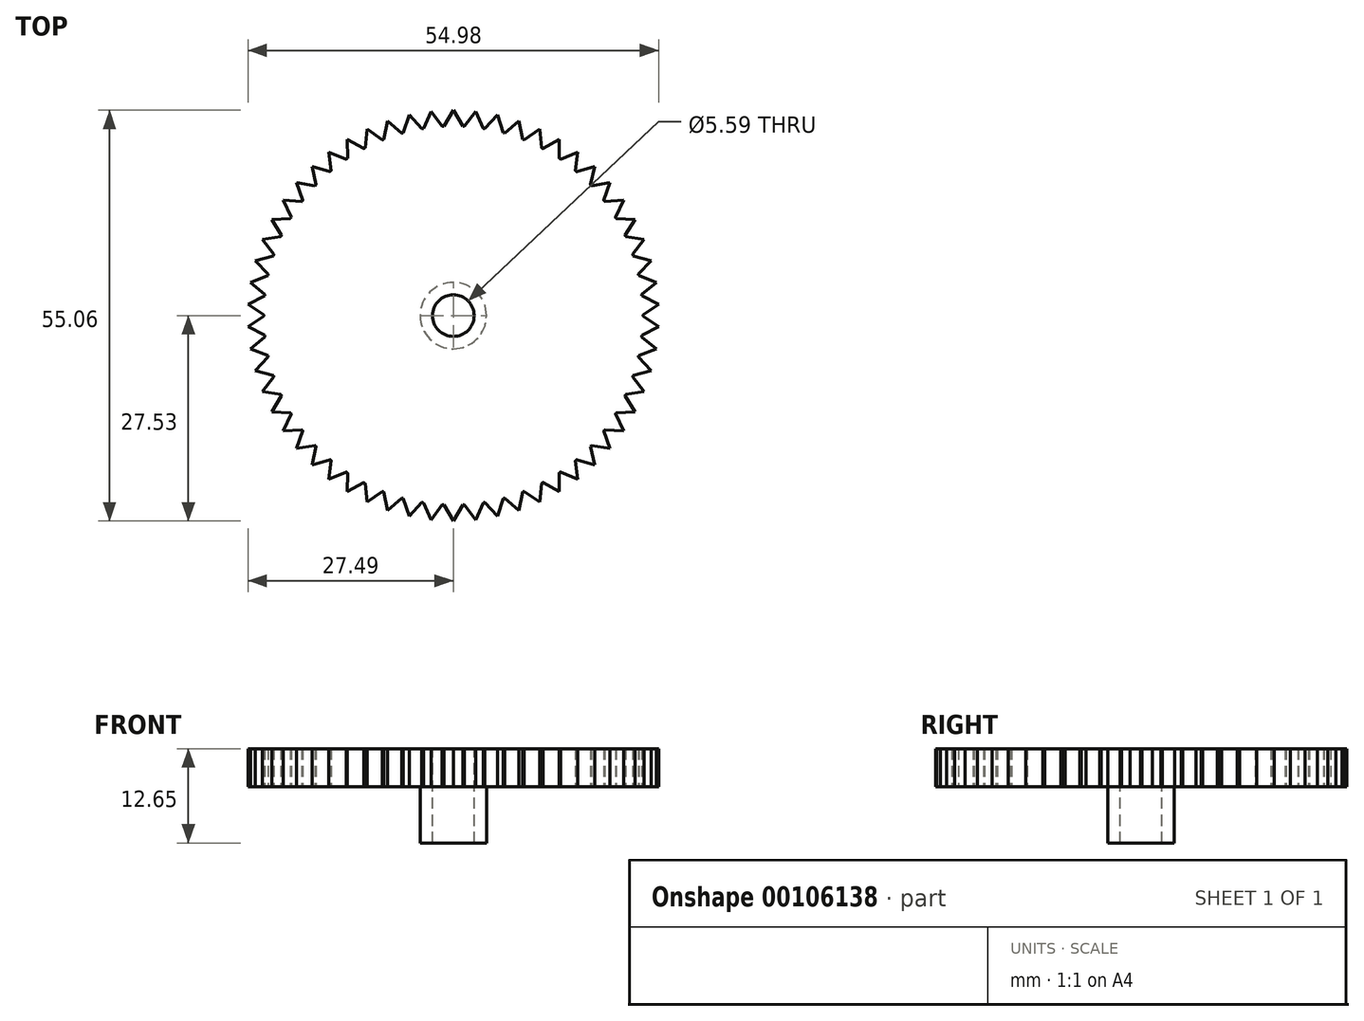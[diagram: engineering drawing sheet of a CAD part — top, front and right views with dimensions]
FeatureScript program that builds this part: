
annotation { "Feature Type Name" : "Feature", "Feature Type Description" : "" }
export const myFeature = defineFeature(function(context is Context, id is Id, definition is map)
    precondition{}
    {
        {
            var Q0;
            Q0=qCreatedBy(makeId("Top.planeOp"),FACE);
            var sketch = newSketch(context, id + "F0", { "sketchPlane" : qUnion([Q0])});
            skCircle(sketch, "E0", {"center": v(0, 0) * mm, "radius": 25.4 * mm});
            skLineSegment(sketch, "E1", {"start": v(-1.27, 25.37) * mm, "end": v(0, 27.53) * mm});
            skLineSegment(sketch, "E2", {"start": v(0, 27.53) * mm, "end": v(1.27, 25.37) * mm});
            skLineSegment(sketch, "E3.1.0", {"start": v(-4, 25.08) * mm, "end": v(-2.98, 27.37) * mm});
            skLineSegment(sketch, "E3.1.1", {"start": v(-2.98, 27.37) * mm, "end": v(-1.48, 25.36) * mm});
            skLineSegment(sketch, "E3.2.0", {"start": v(-6.7, 24.5) * mm, "end": v(-5.92, 26.88) * mm});
            skLineSegment(sketch, "E3.2.1", {"start": v(-5.92, 26.88) * mm, "end": v(-4.21, 25.05) * mm});
            skLineSegment(sketch, "E4.1.3.0", {"start": v(-9.3, 23.63) * mm, "end": v(-8.79, 26.09) * mm});
            skLineSegment(sketch, "E4.3.3.0", {"start": v(-8.79, 26.09) * mm, "end": v(-6.9, 24.45) * mm});
            skLineSegment(sketch, "E4.1.4.0", {"start": v(-11.8, 22.5) * mm, "end": v(-11.56, 24.98) * mm});
            skLineSegment(sketch, "E4.3.4.0", {"start": v(-11.56, 24.98) * mm, "end": v(-9.5, 23.56) * mm});
            skLineSegment(sketch, "E4.1.5.0", {"start": v(-14.17, 21.08) * mm, "end": v(-14.2, 23.59) * mm});
            skLineSegment(sketch, "E4.3.5.0", {"start": v(-14.2, 23.59) * mm, "end": v(-12, 22.4) * mm});
            skLineSegment(sketch, "E4.1.6.0", {"start": v(-16.36, 19.43) * mm, "end": v(-16.66, 21.91) * mm});
            skLineSegment(sketch, "E4.3.6.0", {"start": v(-16.66, 21.91) * mm, "end": v(-14.34, 20.96) * mm});
            skLineSegment(sketch, "E4.1.7.0", {"start": v(-18.37, 17.54) * mm, "end": v(-18.93, 19.99) * mm});
            skLineSegment(sketch, "E4.3.7.0", {"start": v(-18.93, 19.99) * mm, "end": v(-16.52, 19.3) * mm});
            skLineSegment(sketch, "E4.1.8.0", {"start": v(-20.16, 15.46) * mm, "end": v(-20.98, 17.82) * mm});
            skLineSegment(sketch, "E4.3.8.0", {"start": v(-20.98, 17.82) * mm, "end": v(-18.51, 17.4) * mm});
            skLineSegment(sketch, "E4.1.9.0", {"start": v(-21.7, 13.19) * mm, "end": v(-22.78, 15.45) * mm});
            skLineSegment(sketch, "E4.3.9.0", {"start": v(-22.78, 15.45) * mm, "end": v(-20.28, 15.29) * mm});
            skLineSegment(sketch, "E4.1.10.0", {"start": v(-23, 10.76) * mm, "end": v(-24.32, 12.9) * mm});
            skLineSegment(sketch, "E4.3.10.0", {"start": v(-24.32, 12.9) * mm, "end": v(-21.82, 13) * mm});
            skLineSegment(sketch, "E4.1.11.0", {"start": v(-24.04, 8.2) * mm, "end": v(-25.57, 10.19) * mm});
            skLineSegment(sketch, "E4.3.11.0", {"start": v(-25.57, 10.19) * mm, "end": v(-23.1, 10.57) * mm});
            skLineSegment(sketch, "E4.1.12.0", {"start": v(-24.78, 5.56) * mm, "end": v(-26.52, 7.36) * mm});
            skLineSegment(sketch, "E4.3.12.0", {"start": v(-26.52, 7.36) * mm, "end": v(-24.1, 8.01) * mm});
            skLineSegment(sketch, "E4.1.13.0", {"start": v(-25.24, 2.85) * mm, "end": v(-27.17, 4.45) * mm});
            skLineSegment(sketch, "E4.3.13.0", {"start": v(-27.17, 4.45) * mm, "end": v(-24.83, 5.36) * mm});
            skLineSegment(sketch, "E4.1.14.0", {"start": v(-25.4, 0.1) * mm, "end": v(-27.49, 1.5) * mm});
            skLineSegment(sketch, "E4.3.14.0", {"start": v(-27.49, 1.5) * mm, "end": v(-25.26, 2.64) * mm});
            skLineSegment(sketch, "E4.1.15.0", {"start": v(-25.26, -2.64) * mm, "end": v(-27.49, -1.5) * mm});
            skLineSegment(sketch, "E4.3.15.0", {"start": v(-27.49, -1.5) * mm, "end": v(-25.4, -0.1) * mm});
            skLineSegment(sketch, "E4.1.16.0", {"start": v(-24.83, -5.36) * mm, "end": v(-27.17, -4.45) * mm});
            skLineSegment(sketch, "E4.3.16.0", {"start": v(-27.17, -4.45) * mm, "end": v(-25.24, -2.85) * mm});
            skLineSegment(sketch, "E4.1.17.0", {"start": v(-24.1, -8.01) * mm, "end": v(-26.52, -7.36) * mm});
            skLineSegment(sketch, "E4.3.17.0", {"start": v(-26.52, -7.36) * mm, "end": v(-24.78, -5.56) * mm});
            skLineSegment(sketch, "E4.1.18.0", {"start": v(-23.1, -10.57) * mm, "end": v(-25.57, -10.19) * mm});
            skLineSegment(sketch, "E4.3.18.0", {"start": v(-25.57, -10.19) * mm, "end": v(-24.04, -8.2) * mm});
            skLineSegment(sketch, "E4.1.19.0", {"start": v(-21.82, -13) * mm, "end": v(-24.32, -12.9) * mm});
            skLineSegment(sketch, "E4.3.19.0", {"start": v(-24.32, -12.9) * mm, "end": v(-23, -10.76) * mm});
            skLineSegment(sketch, "E4.1.20.0", {"start": v(-20.28, -15.29) * mm, "end": v(-22.78, -15.45) * mm});
            skLineSegment(sketch, "E4.3.20.0", {"start": v(-22.78, -15.45) * mm, "end": v(-21.7, -13.19) * mm});
            skLineSegment(sketch, "E4.1.21.0", {"start": v(-18.51, -17.4) * mm, "end": v(-20.98, -17.82) * mm});
            skLineSegment(sketch, "E4.3.21.0", {"start": v(-20.98, -17.82) * mm, "end": v(-20.16, -15.46) * mm});
            skLineSegment(sketch, "E4.1.22.0", {"start": v(-16.52, -19.3) * mm, "end": v(-18.93, -19.99) * mm});
            skLineSegment(sketch, "E4.3.22.0", {"start": v(-18.93, -19.99) * mm, "end": v(-18.37, -17.54) * mm});
            skLineSegment(sketch, "E4.1.23.0", {"start": v(-14.34, -20.96) * mm, "end": v(-16.66, -21.91) * mm});
            skLineSegment(sketch, "E4.3.23.0", {"start": v(-16.66, -21.91) * mm, "end": v(-16.36, -19.43) * mm});
            skLineSegment(sketch, "E4.1.24.0", {"start": v(-12, -22.4) * mm, "end": v(-14.2, -23.59) * mm});
            skLineSegment(sketch, "E4.3.24.0", {"start": v(-14.2, -23.59) * mm, "end": v(-14.17, -21.08) * mm});
            skLineSegment(sketch, "E4.1.25.0", {"start": v(-9.5, -23.56) * mm, "end": v(-11.56, -24.98) * mm});
            skLineSegment(sketch, "E4.3.25.0", {"start": v(-11.56, -24.98) * mm, "end": v(-11.8, -22.5) * mm});
            skLineSegment(sketch, "E4.1.26.0", {"start": v(-6.9, -24.45) * mm, "end": v(-8.79, -26.09) * mm});
            skLineSegment(sketch, "E4.3.26.0", {"start": v(-8.79, -26.09) * mm, "end": v(-9.3, -23.63) * mm});
            skLineSegment(sketch, "E4.1.27.0", {"start": v(-4.21, -25.05) * mm, "end": v(-5.92, -26.88) * mm});
            skLineSegment(sketch, "E4.3.27.0", {"start": v(-5.92, -26.88) * mm, "end": v(-6.7, -24.5) * mm});
            skLineSegment(sketch, "E4.1.28.0", {"start": v(-1.48, -25.36) * mm, "end": v(-2.98, -27.37) * mm});
            skLineSegment(sketch, "E4.3.28.0", {"start": v(-2.98, -27.37) * mm, "end": v(-4, -25.08) * mm});
            skLineSegment(sketch, "E4.1.29.0", {"start": v(1.27, -25.37) * mm, "end": v(0, -27.53) * mm});
            skLineSegment(sketch, "E4.3.29.0", {"start": v(0, -27.53) * mm, "end": v(-1.27, -25.37) * mm});
            skLineSegment(sketch, "E4.1.30.0", {"start": v(4, -25.08) * mm, "end": v(2.98, -27.37) * mm});
            skLineSegment(sketch, "E4.3.30.0", {"start": v(2.98, -27.37) * mm, "end": v(1.48, -25.36) * mm});
            skLineSegment(sketch, "E4.1.31.0", {"start": v(6.7, -24.5) * mm, "end": v(5.92, -26.88) * mm});
            skLineSegment(sketch, "E4.3.31.0", {"start": v(5.92, -26.88) * mm, "end": v(4.21, -25.05) * mm});
            skLineSegment(sketch, "E4.1.32.0", {"start": v(9.3, -23.63) * mm, "end": v(8.79, -26.09) * mm});
            skLineSegment(sketch, "E4.3.32.0", {"start": v(8.79, -26.09) * mm, "end": v(6.9, -24.45) * mm});
            skLineSegment(sketch, "E4.1.33.0", {"start": v(11.8, -22.5) * mm, "end": v(11.56, -24.98) * mm});
            skLineSegment(sketch, "E4.3.33.0", {"start": v(11.56, -24.98) * mm, "end": v(9.5, -23.56) * mm});
            skLineSegment(sketch, "E4.1.34.0", {"start": v(14.17, -21.08) * mm, "end": v(14.2, -23.59) * mm});
            skLineSegment(sketch, "E4.3.34.0", {"start": v(14.2, -23.59) * mm, "end": v(12, -22.4) * mm});
            skLineSegment(sketch, "E4.1.35.0", {"start": v(16.36, -19.43) * mm, "end": v(16.66, -21.91) * mm});
            skLineSegment(sketch, "E4.3.35.0", {"start": v(16.66, -21.91) * mm, "end": v(14.34, -20.96) * mm});
            skLineSegment(sketch, "E4.1.36.0", {"start": v(18.37, -17.54) * mm, "end": v(18.93, -19.99) * mm});
            skLineSegment(sketch, "E4.3.36.0", {"start": v(18.93, -19.99) * mm, "end": v(16.52, -19.3) * mm});
            skLineSegment(sketch, "E4.1.37.0", {"start": v(20.16, -15.46) * mm, "end": v(20.98, -17.82) * mm});
            skLineSegment(sketch, "E4.3.37.0", {"start": v(20.98, -17.82) * mm, "end": v(18.51, -17.4) * mm});
            skLineSegment(sketch, "E4.1.38.0", {"start": v(21.7, -13.19) * mm, "end": v(22.78, -15.45) * mm});
            skLineSegment(sketch, "E4.3.38.0", {"start": v(22.78, -15.45) * mm, "end": v(20.28, -15.29) * mm});
            skLineSegment(sketch, "E5.1.39.0", {"start": v(23, -10.76) * mm, "end": v(24.32, -12.9) * mm});
            skLineSegment(sketch, "E5.3.39.0", {"start": v(24.32, -12.9) * mm, "end": v(21.82, -13) * mm});
            skLineSegment(sketch, "E5.1.40.0", {"start": v(24.04, -8.2) * mm, "end": v(25.57, -10.19) * mm});
            skLineSegment(sketch, "E5.3.40.0", {"start": v(25.57, -10.19) * mm, "end": v(23.1, -10.57) * mm});
            skLineSegment(sketch, "E5.1.41.0", {"start": v(24.78, -5.56) * mm, "end": v(26.52, -7.36) * mm});
            skLineSegment(sketch, "E5.3.41.0", {"start": v(26.52, -7.36) * mm, "end": v(24.1, -8.01) * mm});
            skLineSegment(sketch, "E5.1.42.0", {"start": v(25.24, -2.85) * mm, "end": v(27.17, -4.45) * mm});
            skLineSegment(sketch, "E5.3.42.0", {"start": v(27.17, -4.45) * mm, "end": v(24.83, -5.36) * mm});
            skLineSegment(sketch, "E5.1.43.0", {"start": v(25.4, -0.1) * mm, "end": v(27.49, -1.5) * mm});
            skLineSegment(sketch, "E5.3.43.0", {"start": v(27.49, -1.5) * mm, "end": v(25.26, -2.64) * mm});
            skLineSegment(sketch, "E5.1.44.0", {"start": v(25.26, 2.64) * mm, "end": v(27.49, 1.5) * mm});
            skLineSegment(sketch, "E5.3.44.0", {"start": v(27.49, 1.5) * mm, "end": v(25.4, 0.1) * mm});
            skLineSegment(sketch, "E6.1.45.0", {"start": v(24.83, 5.36) * mm, "end": v(27.17, 4.45) * mm});
            skLineSegment(sketch, "E6.3.45.0", {"start": v(27.17, 4.45) * mm, "end": v(25.24, 2.85) * mm});
            skLineSegment(sketch, "E6.1.46.0", {"start": v(24.1, 8.01) * mm, "end": v(26.52, 7.36) * mm});
            skLineSegment(sketch, "E6.3.46.0", {"start": v(26.52, 7.36) * mm, "end": v(24.78, 5.56) * mm});
            skLineSegment(sketch, "E7.1.47.0", {"start": v(23.1, 10.57) * mm, "end": v(25.57, 10.19) * mm});
            skLineSegment(sketch, "E7.3.47.0", {"start": v(25.57, 10.19) * mm, "end": v(24.04, 8.2) * mm});
            skLineSegment(sketch, "E7.1.48.0", {"start": v(21.82, 13) * mm, "end": v(24.32, 12.9) * mm});
            skLineSegment(sketch, "E7.3.48.0", {"start": v(24.32, 12.9) * mm, "end": v(23, 10.76) * mm});
            skLineSegment(sketch, "E7.1.49.0", {"start": v(20.28, 15.29) * mm, "end": v(22.78, 15.45) * mm});
            skLineSegment(sketch, "E7.3.49.0", {"start": v(22.78, 15.45) * mm, "end": v(21.7, 13.19) * mm});
            skLineSegment(sketch, "E8.1.50.0", {"start": v(18.51, 17.4) * mm, "end": v(20.98, 17.82) * mm});
            skLineSegment(sketch, "E8.3.50.0", {"start": v(20.98, 17.82) * mm, "end": v(20.16, 15.46) * mm});
            skLineSegment(sketch, "E8.1.51.0", {"start": v(16.52, 19.3) * mm, "end": v(18.93, 19.99) * mm});
            skLineSegment(sketch, "E8.3.51.0", {"start": v(18.93, 19.99) * mm, "end": v(18.37, 17.54) * mm});
            skLineSegment(sketch, "E8.1.52.0", {"start": v(14.34, 20.96) * mm, "end": v(16.66, 21.91) * mm});
            skLineSegment(sketch, "E8.3.52.0", {"start": v(16.66, 21.91) * mm, "end": v(16.36, 19.43) * mm});
            skLineSegment(sketch, "E8.1.53.0", {"start": v(12, 22.4) * mm, "end": v(14.2, 23.59) * mm});
            skLineSegment(sketch, "E8.3.53.0", {"start": v(14.2, 23.59) * mm, "end": v(14.17, 21.08) * mm});
            skLineSegment(sketch, "E8.1.54.0", {"start": v(9.5, 23.56) * mm, "end": v(11.56, 24.98) * mm});
            skLineSegment(sketch, "E8.3.54.0", {"start": v(11.56, 24.98) * mm, "end": v(11.8, 22.5) * mm});
            skLineSegment(sketch, "E9.1.55.0", {"start": v(6.9, 24.45) * mm, "end": v(8.79, 26.09) * mm});
            skLineSegment(sketch, "E9.3.55.0", {"start": v(8.79, 26.09) * mm, "end": v(9.3, 23.63) * mm});
            skLineSegment(sketch, "E9.1.56.0", {"start": v(4.21, 25.05) * mm, "end": v(5.92, 26.88) * mm});
            skLineSegment(sketch, "E9.3.56.0", {"start": v(5.92, 26.88) * mm, "end": v(6.7, 24.5) * mm});
            skLineSegment(sketch, "E10.1.57.0", {"start": v(1.48, 25.36) * mm, "end": v(2.98, 27.37) * mm});
            skLineSegment(sketch, "E10.3.57.0", {"start": v(2.98, 27.37) * mm, "end": v(4, 25.08) * mm});
            skSolve(sketch);
        }
        {
            var Q0;
            {var subQ0=sQuery(id+"F0.wireOp",EDGE,"E4.1.22.0");Q0=makeQuery(id+"F0.imprint","IMPRINT",FACE,{"disambiguationData":[TD([[makeQuery(id+"F0.imprint","IMPRINT",EDGE,{"derivedFrom":subQ0}),-1.0]])]});}
            var Q1;
            {var subQ0=sQuery(id+"F0.wireOp",EDGE,"E4.1.23.0");Q1=makeQuery(id+"F0.imprint","IMPRINT",FACE,{"disambiguationData":[TD([[makeQuery(id+"F0.imprint","IMPRINT",EDGE,{"derivedFrom":subQ0}),-1.0]])]});}
            var Q2;
            {var subQ0=sQuery(id+"F0.wireOp",EDGE,"E4.1.30.0");Q2=makeQuery(id+"F0.imprint","IMPRINT",FACE,{"disambiguationData":[TD([[makeQuery(id+"F0.imprint","IMPRINT",EDGE,{"derivedFrom":subQ0}),-1.0]])]});}
            var Q3;
            {var subQ0=sQuery(id+"F0.wireOp",EDGE,"E4.1.14.0");Q3=makeQuery(id+"F0.imprint","IMPRINT",FACE,{"disambiguationData":[TD([[makeQuery(id+"F0.imprint","IMPRINT",EDGE,{"derivedFrom":subQ0}),-1.0]])]});}
            var Q4;
            {var subQ0=sQuery(id+"F0.wireOp",EDGE,"E4.1.8.0");Q4=makeQuery(id+"F0.imprint","IMPRINT",FACE,{"disambiguationData":[TD([[makeQuery(id+"F0.imprint","IMPRINT",EDGE,{"derivedFrom":subQ0}),-1.0]])]});}
            var Q5;
            {var subQ0=sQuery(id+"F0.wireOp",EDGE,"E3.1.0");Q5=makeQuery(id+"F0.imprint","IMPRINT",FACE,{"disambiguationData":[TD([[makeQuery(id+"F0.imprint","IMPRINT",EDGE,{"derivedFrom":subQ0}),-1.0]])]});}
            var Q6;
            {var subQ0=sQuery(id+"F0.wireOp",EDGE,"E10.1.57.0");Q6=makeQuery(id+"F0.imprint","IMPRINT",FACE,{"disambiguationData":[TD([[makeQuery(id+"F0.imprint","IMPRINT",EDGE,{"derivedFrom":subQ0}),-1.0]])]});}
            var Q7;
            {var subQ0=sQuery(id+"F0.wireOp",EDGE,"E4.1.32.0");Q7=makeQuery(id+"F0.imprint","IMPRINT",FACE,{"disambiguationData":[TD([[makeQuery(id+"F0.imprint","IMPRINT",EDGE,{"derivedFrom":subQ0}),-1.0]])]});}
            var Q8;
            {var subQ0=sQuery(id+"F0.wireOp",EDGE,"E4.1.16.0");Q8=makeQuery(id+"F0.imprint","IMPRINT",FACE,{"disambiguationData":[TD([[makeQuery(id+"F0.imprint","IMPRINT",EDGE,{"derivedFrom":subQ0}),-1.0]])]});}
            var Q9;
            {var subQ0=sQuery(id+"F0.wireOp",EDGE,"E3.2.0");Q9=makeQuery(id+"F0.imprint","IMPRINT",FACE,{"disambiguationData":[TD([[makeQuery(id+"F0.imprint","IMPRINT",EDGE,{"derivedFrom":subQ0}),-1.0]])]});}
            var Q10;
            {var subQ0=sQuery(id+"F0.wireOp",EDGE,"E4.1.34.0");Q10=makeQuery(id+"F0.imprint","IMPRINT",FACE,{"disambiguationData":[TD([[makeQuery(id+"F0.imprint","IMPRINT",EDGE,{"derivedFrom":subQ0}),-1.0]])]});}
            var Q11;
            {var subQ0=sQuery(id+"F0.wireOp",EDGE,"E5.1.44.0");Q11=makeQuery(id+"F0.imprint","IMPRINT",FACE,{"disambiguationData":[TD([[makeQuery(id+"F0.imprint","IMPRINT",EDGE,{"derivedFrom":subQ0}),-1.0]])]});}
            var Q12;
            {var subQ0=sQuery(id+"F0.wireOp",EDGE,"E6.1.46.0");Q12=makeQuery(id+"F0.imprint","IMPRINT",FACE,{"disambiguationData":[TD([[makeQuery(id+"F0.imprint","IMPRINT",EDGE,{"derivedFrom":subQ0}),-1.0]])]});}
            var Q13;
            {var subQ0=sQuery(id+"F0.wireOp",EDGE,"E7.1.49.0");Q13=makeQuery(id+"F0.imprint","IMPRINT",FACE,{"disambiguationData":[TD([[makeQuery(id+"F0.imprint","IMPRINT",EDGE,{"derivedFrom":subQ0}),-1.0]])]});}
            var Q14;
            {var subQ0=sQuery(id+"F0.wireOp",EDGE,"E8.1.52.0");Q14=makeQuery(id+"F0.imprint","IMPRINT",FACE,{"disambiguationData":[TD([[makeQuery(id+"F0.imprint","IMPRINT",EDGE,{"derivedFrom":subQ0}),-1.0]])]});}
            var Q15;
            {var subQ0=sQuery(id+"F0.wireOp",EDGE,"E8.1.54.0");Q15=makeQuery(id+"F0.imprint","IMPRINT",FACE,{"disambiguationData":[TD([[makeQuery(id+"F0.imprint","IMPRINT",EDGE,{"derivedFrom":subQ0}),-1.0]])]});}
            var Q16;
            {var subQ0=sQuery(id+"F0.wireOp",EDGE,"E9.1.55.0");Q16=makeQuery(id+"F0.imprint","IMPRINT",FACE,{"disambiguationData":[TD([[makeQuery(id+"F0.imprint","IMPRINT",EDGE,{"derivedFrom":subQ0}),-1.0]])]});}
            var Q17;
            {var subQ0=sQuery(id+"F0.wireOp",EDGE,"E4.1.24.0");Q17=makeQuery(id+"F0.imprint","IMPRINT",FACE,{"disambiguationData":[TD([[makeQuery(id+"F0.imprint","IMPRINT",EDGE,{"derivedFrom":subQ0}),-1.0]])]});}
            var Q18;
            {var subQ0=sQuery(id+"F0.wireOp",EDGE,"E5.1.41.0");Q18=makeQuery(id+"F0.imprint","IMPRINT",FACE,{"disambiguationData":[TD([[makeQuery(id+"F0.imprint","IMPRINT",EDGE,{"derivedFrom":subQ0}),-1.0]])]});}
            var Q19;
            {var subQ0=sQuery(id+"F0.wireOp",EDGE,"E4.1.25.0");Q19=makeQuery(id+"F0.imprint","IMPRINT",FACE,{"disambiguationData":[TD([[makeQuery(id+"F0.imprint","IMPRINT",EDGE,{"derivedFrom":subQ0}),-1.0]])]});}
            var Q20;
            {var subQ0=sQuery(id+"F0.wireOp",EDGE,"E4.1.9.0");Q20=makeQuery(id+"F0.imprint","IMPRINT",FACE,{"disambiguationData":[TD([[makeQuery(id+"F0.imprint","IMPRINT",EDGE,{"derivedFrom":subQ0}),-1.0]])]});}
            var Q21;
            {var subQ0=sQuery(id+"F0.wireOp",EDGE,"E4.1.3.0");Q21=makeQuery(id+"F0.imprint","IMPRINT",FACE,{"disambiguationData":[TD([[makeQuery(id+"F0.imprint","IMPRINT",EDGE,{"derivedFrom":subQ0}),-1.0]])]});}
            var Q22;
            {var subQ0=sQuery(id+"F0.wireOp",EDGE,"E1");Q22=makeQuery(id+"F0.imprint","IMPRINT",FACE,{"disambiguationData":[TD([[makeQuery(id+"F0.imprint","IMPRINT",EDGE,{"derivedFrom":subQ0}),-1.0]])]});}
            var Q23;
            {var subQ0=sQuery(id+"F0.wireOp",EDGE,"E4.1.35.0");Q23=makeQuery(id+"F0.imprint","IMPRINT",FACE,{"disambiguationData":[TD([[makeQuery(id+"F0.imprint","IMPRINT",EDGE,{"derivedFrom":subQ0}),-1.0]])]});}
            var Q24;
            {var subQ0=sQuery(id+"F0.wireOp",EDGE,"E4.1.19.0");Q24=makeQuery(id+"F0.imprint","IMPRINT",FACE,{"disambiguationData":[TD([[makeQuery(id+"F0.imprint","IMPRINT",EDGE,{"derivedFrom":subQ0}),-1.0]])]});}
            var Q25;
            {var subQ0=sQuery(id+"F0.wireOp",EDGE,"E6.1.45.0");Q25=makeQuery(id+"F0.imprint","IMPRINT",FACE,{"disambiguationData":[TD([[makeQuery(id+"F0.imprint","IMPRINT",EDGE,{"derivedFrom":subQ0}),-1.0]])]});}
            var Q26;
            {var subQ0=sQuery(id+"F0.wireOp",EDGE,"E5.1.42.0");Q26=makeQuery(id+"F0.imprint","IMPRINT",FACE,{"disambiguationData":[TD([[makeQuery(id+"F0.imprint","IMPRINT",EDGE,{"derivedFrom":subQ0}),-1.0]])]});}
            var Q27;
            {var subQ0=sQuery(id+"F0.wireOp",EDGE,"E7.1.48.0");Q27=makeQuery(id+"F0.imprint","IMPRINT",FACE,{"disambiguationData":[TD([[makeQuery(id+"F0.imprint","IMPRINT",EDGE,{"derivedFrom":subQ0}),-1.0]])]});}
            var Q28;
            {var subQ0=sQuery(id+"F0.wireOp",EDGE,"E4.1.26.0");Q28=makeQuery(id+"F0.imprint","IMPRINT",FACE,{"disambiguationData":[TD([[makeQuery(id+"F0.imprint","IMPRINT",EDGE,{"derivedFrom":subQ0}),-1.0]])]});}
            var Q29;
            {var subQ0=sQuery(id+"F0.wireOp",EDGE,"E8.1.51.0");Q29=makeQuery(id+"F0.imprint","IMPRINT",FACE,{"disambiguationData":[TD([[makeQuery(id+"F0.imprint","IMPRINT",EDGE,{"derivedFrom":subQ0}),-1.0]])]});}
            var Q30;
            {var subQ0=sQuery(id+"F0.wireOp",EDGE,"E8.1.53.0");Q30=makeQuery(id+"F0.imprint","IMPRINT",FACE,{"disambiguationData":[TD([[makeQuery(id+"F0.imprint","IMPRINT",EDGE,{"derivedFrom":subQ0}),-1.0]])]});}
            var Q31;
            {var subQ0=sQuery(id+"F0.wireOp",EDGE,"E4.1.4.0");Q31=makeQuery(id+"F0.imprint","IMPRINT",FACE,{"disambiguationData":[TD([[makeQuery(id+"F0.imprint","IMPRINT",EDGE,{"derivedFrom":subQ0}),-1.0]])]});}
            var Q32;
            {var subQ0=sQuery(id+"F0.wireOp",EDGE,"E4.1.36.0");Q32=makeQuery(id+"F0.imprint","IMPRINT",FACE,{"disambiguationData":[TD([[makeQuery(id+"F0.imprint","IMPRINT",EDGE,{"derivedFrom":subQ0}),-1.0]])]});}
            var Q33;
            {var subQ0=sQuery(id+"F0.wireOp",EDGE,"E4.1.20.0");Q33=makeQuery(id+"F0.imprint","IMPRINT",FACE,{"disambiguationData":[TD([[makeQuery(id+"F0.imprint","IMPRINT",EDGE,{"derivedFrom":subQ0}),-1.0]])]});}
            var Q34;
            {var subQ0=sQuery(id+"F0.wireOp",EDGE,"E9.1.56.0");Q34=makeQuery(id+"F0.imprint","IMPRINT",FACE,{"disambiguationData":[TD([[makeQuery(id+"F0.imprint","IMPRINT",EDGE,{"derivedFrom":subQ0}),-1.0]])]});}
            var Q35;
            {var subQ0=sQuery(id+"F0.wireOp",EDGE,"E4.1.17.0");Q35=makeQuery(id+"F0.imprint","IMPRINT",FACE,{"disambiguationData":[TD([[makeQuery(id+"F0.imprint","IMPRINT",EDGE,{"derivedFrom":subQ0}),-1.0]])]});}
            var Q36;
            {var subQ0=sQuery(id+"F0.wireOp",EDGE,"E5.1.43.0");Q36=makeQuery(id+"F0.imprint","IMPRINT",FACE,{"disambiguationData":[TD([[makeQuery(id+"F0.imprint","IMPRINT",EDGE,{"derivedFrom":subQ0}),-1.0]])]});}
            var Q37;
            {var subQ0=sQuery(id+"F0.wireOp",EDGE,"E5.1.39.0");Q37=makeQuery(id+"F0.imprint","IMPRINT",FACE,{"disambiguationData":[TD([[makeQuery(id+"F0.imprint","IMPRINT",EDGE,{"derivedFrom":subQ0}),-1.0]])]});}
            var Q38;
            {var subQ0=sQuery(id+"F0.wireOp",EDGE,"E4.1.7.0");Q38=makeQuery(id+"F0.imprint","IMPRINT",FACE,{"disambiguationData":[TD([[makeQuery(id+"F0.imprint","IMPRINT",EDGE,{"derivedFrom":subQ0}),-1.0]])]});}
            var Q39;
            {var subQ0=sQuery(id+"F0.wireOp",EDGE,"E4.1.12.0");Q39=makeQuery(id+"F0.imprint","IMPRINT",FACE,{"disambiguationData":[TD([[makeQuery(id+"F0.imprint","IMPRINT",EDGE,{"derivedFrom":subQ0}),-1.0]])]});}
            var Q40;
            {var subQ0=sQuery(id+"F0.wireOp",EDGE,"E4.1.28.0");Q40=makeQuery(id+"F0.imprint","IMPRINT",FACE,{"disambiguationData":[TD([[makeQuery(id+"F0.imprint","IMPRINT",EDGE,{"derivedFrom":subQ0}),-1.0]])]});}
            var Q41;
            {var subQ0=sQuery(id+"F0.wireOp",EDGE,"E0");var subQ91=makeQuery(id+"F0.imprint","INTERSECT",VERTEX,{"derivedFrom":[subQ0,sQuery(id+"F0.wireOp",EDGE,"E5.1.44.0")]});Q41=makeQuery(id+"F0.imprint","IMPRINT",FACE,{"disambiguationData":[TD([[makeQuery(id+"F0.imprint","IMPRINT",EDGE,{"disambiguationData":[TD([[subQ91,1.0]])],"derivedFrom":subQ0}),1.0]])]});}
            var Q42;
            {var subQ0=sQuery(id+"F0.wireOp",EDGE,"E4.1.13.0");Q42=makeQuery(id+"F0.imprint","IMPRINT",FACE,{"disambiguationData":[TD([[makeQuery(id+"F0.imprint","IMPRINT",EDGE,{"derivedFrom":subQ0}),-1.0]])]});}
            var Q43;
            {var subQ0=sQuery(id+"F0.wireOp",EDGE,"E4.1.29.0");Q43=makeQuery(id+"F0.imprint","IMPRINT",FACE,{"disambiguationData":[TD([[makeQuery(id+"F0.imprint","IMPRINT",EDGE,{"derivedFrom":subQ0}),-1.0]])]});}
            var Q44;
            {var subQ0=sQuery(id+"F0.wireOp",EDGE,"E4.1.5.0");Q44=makeQuery(id+"F0.imprint","IMPRINT",FACE,{"disambiguationData":[TD([[makeQuery(id+"F0.imprint","IMPRINT",EDGE,{"derivedFrom":subQ0}),-1.0]])]});}
            var Q45;
            {var subQ0=sQuery(id+"F0.wireOp",EDGE,"E4.1.10.0");Q45=makeQuery(id+"F0.imprint","IMPRINT",FACE,{"disambiguationData":[TD([[makeQuery(id+"F0.imprint","IMPRINT",EDGE,{"derivedFrom":subQ0}),-1.0]])]});}
            var Q46;
            {var subQ0=sQuery(id+"F0.wireOp",EDGE,"E4.1.15.0");Q46=makeQuery(id+"F0.imprint","IMPRINT",FACE,{"disambiguationData":[TD([[makeQuery(id+"F0.imprint","IMPRINT",EDGE,{"derivedFrom":subQ0}),-1.0]])]});}
            var Q47;
            {var subQ0=sQuery(id+"F0.wireOp",EDGE,"E4.1.38.0");Q47=makeQuery(id+"F0.imprint","IMPRINT",FACE,{"disambiguationData":[TD([[makeQuery(id+"F0.imprint","IMPRINT",EDGE,{"derivedFrom":subQ0}),-1.0]])]});}
            var Q48;
            {var subQ0=sQuery(id+"F0.wireOp",EDGE,"E4.1.31.0");Q48=makeQuery(id+"F0.imprint","IMPRINT",FACE,{"disambiguationData":[TD([[makeQuery(id+"F0.imprint","IMPRINT",EDGE,{"derivedFrom":subQ0}),-1.0]])]});}
            var Q49;
            {var subQ0=sQuery(id+"F0.wireOp",EDGE,"E4.1.6.0");Q49=makeQuery(id+"F0.imprint","IMPRINT",FACE,{"disambiguationData":[TD([[makeQuery(id+"F0.imprint","IMPRINT",EDGE,{"derivedFrom":subQ0}),-1.0]])]});}
            var Q50;
            {var subQ0=sQuery(id+"F0.wireOp",EDGE,"E4.1.27.0");Q50=makeQuery(id+"F0.imprint","IMPRINT",FACE,{"disambiguationData":[TD([[makeQuery(id+"F0.imprint","IMPRINT",EDGE,{"derivedFrom":subQ0}),-1.0]])]});}
            var Q51;
            {var subQ0=sQuery(id+"F0.wireOp",EDGE,"E4.1.33.0");Q51=makeQuery(id+"F0.imprint","IMPRINT",FACE,{"disambiguationData":[TD([[makeQuery(id+"F0.imprint","IMPRINT",EDGE,{"derivedFrom":subQ0}),-1.0]])]});}
            var Q52;
            {var subQ0=sQuery(id+"F0.wireOp",EDGE,"E4.1.21.0");Q52=makeQuery(id+"F0.imprint","IMPRINT",FACE,{"disambiguationData":[TD([[makeQuery(id+"F0.imprint","IMPRINT",EDGE,{"derivedFrom":subQ0}),-1.0]])]});}
            var Q53;
            {var subQ0=sQuery(id+"F0.wireOp",EDGE,"E4.1.18.0");Q53=makeQuery(id+"F0.imprint","IMPRINT",FACE,{"disambiguationData":[TD([[makeQuery(id+"F0.imprint","IMPRINT",EDGE,{"derivedFrom":subQ0}),-1.0]])]});}
            var Q54;
            {var subQ0=sQuery(id+"F0.wireOp",EDGE,"E7.1.47.0");Q54=makeQuery(id+"F0.imprint","IMPRINT",FACE,{"disambiguationData":[TD([[makeQuery(id+"F0.imprint","IMPRINT",EDGE,{"derivedFrom":subQ0}),-1.0]])]});}
            var Q55;
            {var subQ0=sQuery(id+"F0.wireOp",EDGE,"E8.1.50.0");Q55=makeQuery(id+"F0.imprint","IMPRINT",FACE,{"disambiguationData":[TD([[makeQuery(id+"F0.imprint","IMPRINT",EDGE,{"derivedFrom":subQ0}),-1.0]])]});}
            var Q56;
            {var subQ0=sQuery(id+"F0.wireOp",EDGE,"E5.1.40.0");Q56=makeQuery(id+"F0.imprint","IMPRINT",FACE,{"disambiguationData":[TD([[makeQuery(id+"F0.imprint","IMPRINT",EDGE,{"derivedFrom":subQ0}),-1.0]])]});}
            var Q57;
            {var subQ0=sQuery(id+"F0.wireOp",EDGE,"E4.1.37.0");Q57=makeQuery(id+"F0.imprint","IMPRINT",FACE,{"disambiguationData":[TD([[makeQuery(id+"F0.imprint","IMPRINT",EDGE,{"derivedFrom":subQ0}),-1.0]])]});}
            var Q58;
            {var subQ0=sQuery(id+"F0.wireOp",EDGE,"E4.1.11.0");Q58=makeQuery(id+"F0.imprint","IMPRINT",FACE,{"disambiguationData":[TD([[makeQuery(id+"F0.imprint","IMPRINT",EDGE,{"derivedFrom":subQ0}),-1.0]])]});}
            extrude(context, id + "F1", {"entities" : qUnion([Q0, Q1, Q2, Q3, Q4, Q5, Q6, Q7, Q8, Q9, Q10, Q11, Q12, Q13, Q14, Q15, Q16, Q17, Q18, Q19, Q20, Q21, Q22, Q23, Q24, Q25, Q26, Q27, Q28, Q29, Q30, Q31, Q32, Q33, Q34, Q35, Q36, Q37, Q38, Q39, Q40, Q41, Q42, Q43, Q44, Q45, Q46, Q47, Q48, Q49, Q50, Q51, Q52, Q53, Q54, Q55, Q56, Q57, Q58]), "depth" : 5.08 * mm});
        }
        {
            var Q0;
            Q0=makeQuery(id+"F1.opExtrude","CAP_FACE",FACE,{"disambiguationData":[OSD([sQuery(id+"F0.wireOp",EDGE,"E0"),sQuery(id+"F0.wireOp",EDGE,"E1"),sQuery(id+"F0.wireOp",EDGE,"E2"),sQuery(id+"F0.wireOp",EDGE,"E3.1.0"),sQuery(id+"F0.wireOp",EDGE,"E3.1.1"),sQuery(id+"F0.wireOp",EDGE,"E3.2.0"),sQuery(id+"F0.wireOp",EDGE,"E3.2.1"),sQuery(id+"F0.wireOp",EDGE,"E4.1.3.0"),sQuery(id+"F0.wireOp",EDGE,"E4.3.3.0"),sQuery(id+"F0.wireOp",EDGE,"E4.1.4.0"),sQuery(id+"F0.wireOp",EDGE,"E4.3.4.0"),sQuery(id+"F0.wireOp",EDGE,"E4.1.5.0"),sQuery(id+"F0.wireOp",EDGE,"E4.3.5.0"),sQuery(id+"F0.wireOp",EDGE,"E4.1.6.0"),sQuery(id+"F0.wireOp",EDGE,"E4.3.6.0"),sQuery(id+"F0.wireOp",EDGE,"E4.1.7.0"),sQuery(id+"F0.wireOp",EDGE,"E4.3.7.0"),sQuery(id+"F0.wireOp",EDGE,"E4.1.8.0"),sQuery(id+"F0.wireOp",EDGE,"E4.3.8.0"),sQuery(id+"F0.wireOp",EDGE,"E4.1.9.0"),sQuery(id+"F0.wireOp",EDGE,"E4.3.9.0"),sQuery(id+"F0.wireOp",EDGE,"E4.1.10.0"),sQuery(id+"F0.wireOp",EDGE,"E4.3.10.0"),sQuery(id+"F0.wireOp",EDGE,"E4.1.11.0"),sQuery(id+"F0.wireOp",EDGE,"E4.3.11.0"),sQuery(id+"F0.wireOp",EDGE,"E4.1.12.0"),sQuery(id+"F0.wireOp",EDGE,"E4.3.12.0"),sQuery(id+"F0.wireOp",EDGE,"E4.1.13.0"),sQuery(id+"F0.wireOp",EDGE,"E4.3.13.0"),sQuery(id+"F0.wireOp",EDGE,"E4.1.14.0"),sQuery(id+"F0.wireOp",EDGE,"E4.3.14.0"),sQuery(id+"F0.wireOp",EDGE,"E4.1.15.0"),sQuery(id+"F0.wireOp",EDGE,"E4.3.15.0"),sQuery(id+"F0.wireOp",EDGE,"E4.1.16.0"),sQuery(id+"F0.wireOp",EDGE,"E4.3.16.0"),sQuery(id+"F0.wireOp",EDGE,"E4.1.17.0"),sQuery(id+"F0.wireOp",EDGE,"E4.3.17.0"),sQuery(id+"F0.wireOp",EDGE,"E4.1.18.0"),sQuery(id+"F0.wireOp",EDGE,"E4.3.18.0"),sQuery(id+"F0.wireOp",EDGE,"E4.1.19.0"),sQuery(id+"F0.wireOp",EDGE,"E4.3.19.0"),sQuery(id+"F0.wireOp",EDGE,"E4.1.20.0"),sQuery(id+"F0.wireOp",EDGE,"E4.3.20.0"),sQuery(id+"F0.wireOp",EDGE,"E4.1.21.0"),sQuery(id+"F0.wireOp",EDGE,"E4.3.21.0"),sQuery(id+"F0.wireOp",EDGE,"E4.1.22.0"),sQuery(id+"F0.wireOp",EDGE,"E4.3.22.0"),sQuery(id+"F0.wireOp",EDGE,"E4.1.23.0"),sQuery(id+"F0.wireOp",EDGE,"E4.3.23.0"),sQuery(id+"F0.wireOp",EDGE,"E4.1.24.0"),sQuery(id+"F0.wireOp",EDGE,"E4.3.24.0"),sQuery(id+"F0.wireOp",EDGE,"E4.1.25.0"),sQuery(id+"F0.wireOp",EDGE,"E4.3.25.0"),sQuery(id+"F0.wireOp",EDGE,"E4.1.26.0"),sQuery(id+"F0.wireOp",EDGE,"E4.3.26.0"),sQuery(id+"F0.wireOp",EDGE,"E4.1.27.0"),sQuery(id+"F0.wireOp",EDGE,"E4.3.27.0"),sQuery(id+"F0.wireOp",EDGE,"E4.1.28.0"),sQuery(id+"F0.wireOp",EDGE,"E4.3.28.0"),sQuery(id+"F0.wireOp",EDGE,"E4.1.29.0"),sQuery(id+"F0.wireOp",EDGE,"E4.3.29.0"),sQuery(id+"F0.wireOp",EDGE,"E4.1.30.0"),sQuery(id+"F0.wireOp",EDGE,"E4.3.30.0"),sQuery(id+"F0.wireOp",EDGE,"E4.1.31.0"),sQuery(id+"F0.wireOp",EDGE,"E4.3.31.0"),sQuery(id+"F0.wireOp",EDGE,"E4.1.32.0"),sQuery(id+"F0.wireOp",EDGE,"E4.3.32.0"),sQuery(id+"F0.wireOp",EDGE,"E4.1.33.0"),sQuery(id+"F0.wireOp",EDGE,"E4.3.33.0"),sQuery(id+"F0.wireOp",EDGE,"E4.1.34.0"),sQuery(id+"F0.wireOp",EDGE,"E4.3.34.0"),sQuery(id+"F0.wireOp",EDGE,"E4.1.35.0"),sQuery(id+"F0.wireOp",EDGE,"E4.3.35.0"),sQuery(id+"F0.wireOp",EDGE,"E4.1.36.0"),sQuery(id+"F0.wireOp",EDGE,"E4.3.36.0"),sQuery(id+"F0.wireOp",EDGE,"E4.1.37.0"),sQuery(id+"F0.wireOp",EDGE,"E4.3.37.0"),sQuery(id+"F0.wireOp",EDGE,"E4.1.38.0"),sQuery(id+"F0.wireOp",EDGE,"E4.3.38.0"),sQuery(id+"F0.wireOp",EDGE,"E5.1.39.0"),sQuery(id+"F0.wireOp",EDGE,"E5.3.39.0"),sQuery(id+"F0.wireOp",EDGE,"E5.1.40.0"),sQuery(id+"F0.wireOp",EDGE,"E5.3.40.0"),sQuery(id+"F0.wireOp",EDGE,"E5.1.41.0"),sQuery(id+"F0.wireOp",EDGE,"E5.3.41.0"),sQuery(id+"F0.wireOp",EDGE,"E5.1.42.0"),sQuery(id+"F0.wireOp",EDGE,"E5.3.42.0"),sQuery(id+"F0.wireOp",EDGE,"E5.1.43.0"),sQuery(id+"F0.wireOp",EDGE,"E5.3.43.0"),sQuery(id+"F0.wireOp",EDGE,"E5.1.44.0"),sQuery(id+"F0.wireOp",EDGE,"E5.3.44.0"),sQuery(id+"F0.wireOp",EDGE,"E6.1.45.0"),sQuery(id+"F0.wireOp",EDGE,"E6.3.45.0"),sQuery(id+"F0.wireOp",EDGE,"E6.1.46.0"),sQuery(id+"F0.wireOp",EDGE,"E6.3.46.0"),sQuery(id+"F0.wireOp",EDGE,"E7.1.47.0"),sQuery(id+"F0.wireOp",EDGE,"E7.3.47.0"),sQuery(id+"F0.wireOp",EDGE,"E7.1.48.0"),sQuery(id+"F0.wireOp",EDGE,"E7.3.48.0"),sQuery(id+"F0.wireOp",EDGE,"E7.1.49.0"),sQuery(id+"F0.wireOp",EDGE,"E7.3.49.0"),sQuery(id+"F0.wireOp",EDGE,"E8.1.50.0"),sQuery(id+"F0.wireOp",EDGE,"E8.3.50.0"),sQuery(id+"F0.wireOp",EDGE,"E8.1.51.0"),sQuery(id+"F0.wireOp",EDGE,"E8.3.51.0"),sQuery(id+"F0.wireOp",EDGE,"E8.1.52.0"),sQuery(id+"F0.wireOp",EDGE,"E8.3.52.0"),sQuery(id+"F0.wireOp",EDGE,"E8.1.53.0"),sQuery(id+"F0.wireOp",EDGE,"E8.3.53.0"),sQuery(id+"F0.wireOp",EDGE,"E8.1.54.0"),sQuery(id+"F0.wireOp",EDGE,"E8.3.54.0"),sQuery(id+"F0.wireOp",EDGE,"E9.1.55.0"),sQuery(id+"F0.wireOp",EDGE,"E9.3.55.0"),sQuery(id+"F0.wireOp",EDGE,"E9.1.56.0"),sQuery(id+"F0.wireOp",EDGE,"E9.3.56.0"),sQuery(id+"F0.wireOp",EDGE,"E10.1.57.0"),sQuery(id+"F0.wireOp",EDGE,"E10.3.57.0")])],"isStart":false});
            var sketch = newSketch(context, id + "F2", { "sketchPlane" : qUnion([Q0])});
            skCircle(sketch, "E11", {"center": v(0, 0) * mm, "radius": 2.8 * mm});
            skSolve(sketch);
        }
        {
            var Q0;
            Q0 = qSketchRegion(id + "F2", true);
            extrude(context, id + "F3", {"entities" : qUnion([Q0]), "operationType" : NewBodyOperationType.REMOVE, "oppositeDirection" : true, "depth" : 5.08 * mm});
        }
        {
            var Q0;
            Q0=makeQuery(id+"F1.opExtrude","CAP_FACE",FACE,{"disambiguationData":[OSD([sQuery(id+"F0.wireOp",EDGE,"E0"),sQuery(id+"F0.wireOp",EDGE,"E1"),sQuery(id+"F0.wireOp",EDGE,"E2"),sQuery(id+"F0.wireOp",EDGE,"E3.1.0"),sQuery(id+"F0.wireOp",EDGE,"E3.1.1"),sQuery(id+"F0.wireOp",EDGE,"E3.2.0"),sQuery(id+"F0.wireOp",EDGE,"E3.2.1"),sQuery(id+"F0.wireOp",EDGE,"E4.1.3.0"),sQuery(id+"F0.wireOp",EDGE,"E4.3.3.0"),sQuery(id+"F0.wireOp",EDGE,"E4.1.4.0"),sQuery(id+"F0.wireOp",EDGE,"E4.3.4.0"),sQuery(id+"F0.wireOp",EDGE,"E4.1.5.0"),sQuery(id+"F0.wireOp",EDGE,"E4.3.5.0"),sQuery(id+"F0.wireOp",EDGE,"E4.1.6.0"),sQuery(id+"F0.wireOp",EDGE,"E4.3.6.0"),sQuery(id+"F0.wireOp",EDGE,"E4.1.7.0"),sQuery(id+"F0.wireOp",EDGE,"E4.3.7.0"),sQuery(id+"F0.wireOp",EDGE,"E4.1.8.0"),sQuery(id+"F0.wireOp",EDGE,"E4.3.8.0"),sQuery(id+"F0.wireOp",EDGE,"E4.1.9.0"),sQuery(id+"F0.wireOp",EDGE,"E4.3.9.0"),sQuery(id+"F0.wireOp",EDGE,"E4.1.10.0"),sQuery(id+"F0.wireOp",EDGE,"E4.3.10.0"),sQuery(id+"F0.wireOp",EDGE,"E4.1.11.0"),sQuery(id+"F0.wireOp",EDGE,"E4.3.11.0"),sQuery(id+"F0.wireOp",EDGE,"E4.1.12.0"),sQuery(id+"F0.wireOp",EDGE,"E4.3.12.0"),sQuery(id+"F0.wireOp",EDGE,"E4.1.13.0"),sQuery(id+"F0.wireOp",EDGE,"E4.3.13.0"),sQuery(id+"F0.wireOp",EDGE,"E4.1.14.0"),sQuery(id+"F0.wireOp",EDGE,"E4.3.14.0"),sQuery(id+"F0.wireOp",EDGE,"E4.1.15.0"),sQuery(id+"F0.wireOp",EDGE,"E4.3.15.0"),sQuery(id+"F0.wireOp",EDGE,"E4.1.16.0"),sQuery(id+"F0.wireOp",EDGE,"E4.3.16.0"),sQuery(id+"F0.wireOp",EDGE,"E4.1.17.0"),sQuery(id+"F0.wireOp",EDGE,"E4.3.17.0"),sQuery(id+"F0.wireOp",EDGE,"E4.1.18.0"),sQuery(id+"F0.wireOp",EDGE,"E4.3.18.0"),sQuery(id+"F0.wireOp",EDGE,"E4.1.19.0"),sQuery(id+"F0.wireOp",EDGE,"E4.3.19.0"),sQuery(id+"F0.wireOp",EDGE,"E4.1.20.0"),sQuery(id+"F0.wireOp",EDGE,"E4.3.20.0"),sQuery(id+"F0.wireOp",EDGE,"E4.1.21.0"),sQuery(id+"F0.wireOp",EDGE,"E4.3.21.0"),sQuery(id+"F0.wireOp",EDGE,"E4.1.22.0"),sQuery(id+"F0.wireOp",EDGE,"E4.3.22.0"),sQuery(id+"F0.wireOp",EDGE,"E4.1.23.0"),sQuery(id+"F0.wireOp",EDGE,"E4.3.23.0"),sQuery(id+"F0.wireOp",EDGE,"E4.1.24.0"),sQuery(id+"F0.wireOp",EDGE,"E4.3.24.0"),sQuery(id+"F0.wireOp",EDGE,"E4.1.25.0"),sQuery(id+"F0.wireOp",EDGE,"E4.3.25.0"),sQuery(id+"F0.wireOp",EDGE,"E4.1.26.0"),sQuery(id+"F0.wireOp",EDGE,"E4.3.26.0"),sQuery(id+"F0.wireOp",EDGE,"E4.1.27.0"),sQuery(id+"F0.wireOp",EDGE,"E4.3.27.0"),sQuery(id+"F0.wireOp",EDGE,"E4.1.28.0"),sQuery(id+"F0.wireOp",EDGE,"E4.3.28.0"),sQuery(id+"F0.wireOp",EDGE,"E4.1.29.0"),sQuery(id+"F0.wireOp",EDGE,"E4.3.29.0"),sQuery(id+"F0.wireOp",EDGE,"E4.1.30.0"),sQuery(id+"F0.wireOp",EDGE,"E4.3.30.0"),sQuery(id+"F0.wireOp",EDGE,"E4.1.31.0"),sQuery(id+"F0.wireOp",EDGE,"E4.3.31.0"),sQuery(id+"F0.wireOp",EDGE,"E4.1.32.0"),sQuery(id+"F0.wireOp",EDGE,"E4.3.32.0"),sQuery(id+"F0.wireOp",EDGE,"E4.1.33.0"),sQuery(id+"F0.wireOp",EDGE,"E4.3.33.0"),sQuery(id+"F0.wireOp",EDGE,"E4.1.34.0"),sQuery(id+"F0.wireOp",EDGE,"E4.3.34.0"),sQuery(id+"F0.wireOp",EDGE,"E4.1.35.0"),sQuery(id+"F0.wireOp",EDGE,"E4.3.35.0"),sQuery(id+"F0.wireOp",EDGE,"E4.1.36.0"),sQuery(id+"F0.wireOp",EDGE,"E4.3.36.0"),sQuery(id+"F0.wireOp",EDGE,"E4.1.37.0"),sQuery(id+"F0.wireOp",EDGE,"E4.3.37.0"),sQuery(id+"F0.wireOp",EDGE,"E4.1.38.0"),sQuery(id+"F0.wireOp",EDGE,"E4.3.38.0"),sQuery(id+"F0.wireOp",EDGE,"E5.1.39.0"),sQuery(id+"F0.wireOp",EDGE,"E5.3.39.0"),sQuery(id+"F0.wireOp",EDGE,"E5.1.40.0"),sQuery(id+"F0.wireOp",EDGE,"E5.3.40.0"),sQuery(id+"F0.wireOp",EDGE,"E5.1.41.0"),sQuery(id+"F0.wireOp",EDGE,"E5.3.41.0"),sQuery(id+"F0.wireOp",EDGE,"E5.1.42.0"),sQuery(id+"F0.wireOp",EDGE,"E5.3.42.0"),sQuery(id+"F0.wireOp",EDGE,"E5.1.43.0"),sQuery(id+"F0.wireOp",EDGE,"E5.3.43.0"),sQuery(id+"F0.wireOp",EDGE,"E5.1.44.0"),sQuery(id+"F0.wireOp",EDGE,"E5.3.44.0"),sQuery(id+"F0.wireOp",EDGE,"E6.1.45.0"),sQuery(id+"F0.wireOp",EDGE,"E6.3.45.0"),sQuery(id+"F0.wireOp",EDGE,"E6.1.46.0"),sQuery(id+"F0.wireOp",EDGE,"E6.3.46.0"),sQuery(id+"F0.wireOp",EDGE,"E7.1.47.0"),sQuery(id+"F0.wireOp",EDGE,"E7.3.47.0"),sQuery(id+"F0.wireOp",EDGE,"E7.1.48.0"),sQuery(id+"F0.wireOp",EDGE,"E7.3.48.0"),sQuery(id+"F0.wireOp",EDGE,"E7.1.49.0"),sQuery(id+"F0.wireOp",EDGE,"E7.3.49.0"),sQuery(id+"F0.wireOp",EDGE,"E8.1.50.0"),sQuery(id+"F0.wireOp",EDGE,"E8.3.50.0"),sQuery(id+"F0.wireOp",EDGE,"E8.1.51.0"),sQuery(id+"F0.wireOp",EDGE,"E8.3.51.0"),sQuery(id+"F0.wireOp",EDGE,"E8.1.52.0"),sQuery(id+"F0.wireOp",EDGE,"E8.3.52.0"),sQuery(id+"F0.wireOp",EDGE,"E8.1.53.0"),sQuery(id+"F0.wireOp",EDGE,"E8.3.53.0"),sQuery(id+"F0.wireOp",EDGE,"E8.1.54.0"),sQuery(id+"F0.wireOp",EDGE,"E8.3.54.0"),sQuery(id+"F0.wireOp",EDGE,"E9.1.55.0"),sQuery(id+"F0.wireOp",EDGE,"E9.3.55.0"),sQuery(id+"F0.wireOp",EDGE,"E9.1.56.0"),sQuery(id+"F0.wireOp",EDGE,"E9.3.56.0"),sQuery(id+"F0.wireOp",EDGE,"E10.1.57.0"),sQuery(id+"F0.wireOp",EDGE,"E10.3.57.0")])],"isStart":true});
            var sketch = newSketch(context, id + "F4", { "sketchPlane" : qUnion([Q0])});
            skCircle(sketch, "E12", {"center": v(0, 0) * mm, "radius": 4.45 * mm});
            skSolve(sketch);
        }
        {
            var Q0;
            Q0=makeQuery(id+"F4.imprint","IMPRINT",FACE,{"disambiguationData":[TD([[makeQuery(id+"F4.imprint","IMPRINT",EDGE,{"derivedFrom":sQuery(id+"F4.wireOp",EDGE,"E12")}),1.0]])]});
            extrude(context, id + "F5", {"entities" : qUnion([Q0]), "operationType" : NewBodyOperationType.ADD, "depth" : 7.57 * mm});
        }
    });
